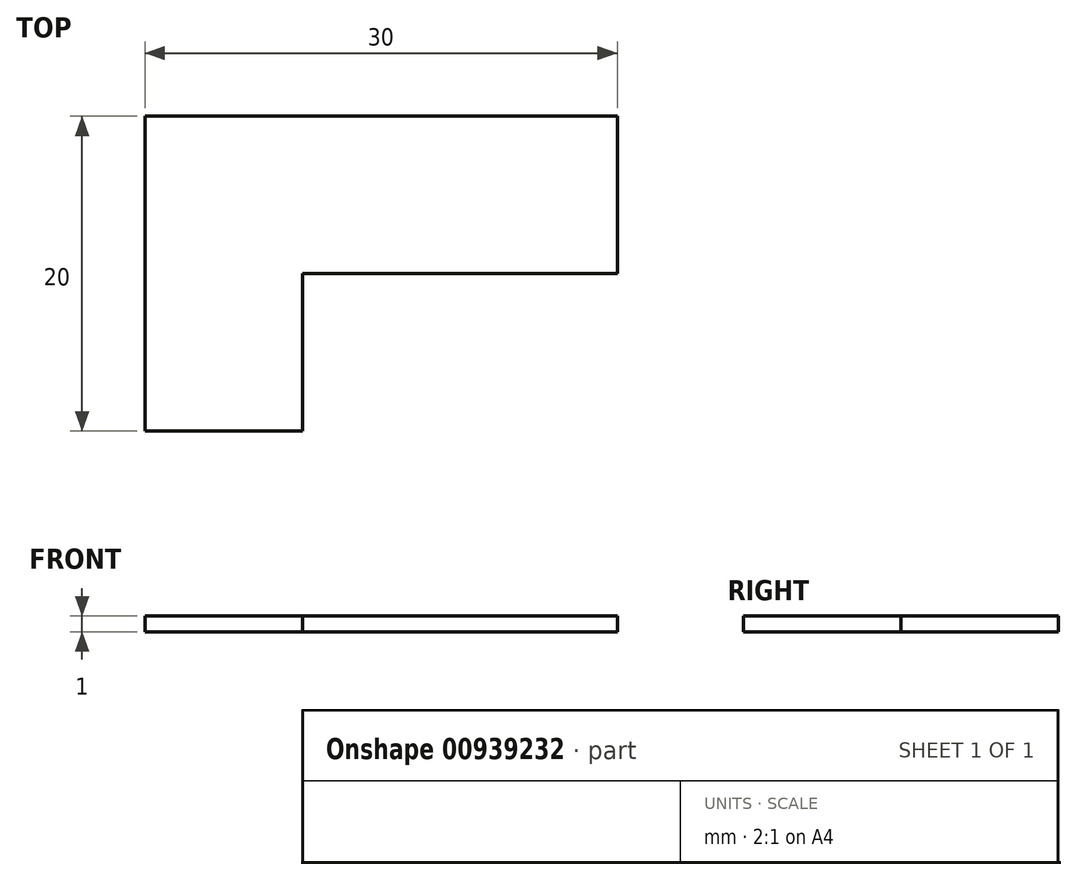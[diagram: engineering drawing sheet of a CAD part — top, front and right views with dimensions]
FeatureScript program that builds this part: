
annotation { "Feature Type Name" : "Feature", "Feature Type Description" : "" }
export const myFeature = defineFeature(function(context is Context, id is Id, definition is map)
    precondition{}
    {
        {
            var Q0;
            Q0=qCreatedBy(makeId("Top.planeOp"),FACE);
            var sketch = newSketch(context, id + "F0", { "sketchPlane" : qUnion([Q0])});
            skLineSegment(sketch, "E0", {"start": v(0, 0) * mm, "end": v(20, 0) * mm});
            skLineSegment(sketch, "E1", {"start": v(20, 0) * mm, "end": v(20, 10) * mm});
            skLineSegment(sketch, "E2", {"start": v(20, 10) * mm, "end": v(-10, 10) * mm});
            skLineSegment(sketch, "E3", {"start": v(-10, 10) * mm, "end": v(-10, -10) * mm});
            skLineSegment(sketch, "E4", {"start": v(-10, -10) * mm, "end": v(0, -10) * mm});
            skLineSegment(sketch, "E5", {"start": v(0, -10) * mm, "end": v(0, 0) * mm});
            skSolve(sketch);
        }
        {
            var Q0;
            Q0=makeQuery(id+"F0.imprint","IMPRINT",FACE,{"disambiguationData":[TD([[makeQuery(id+"F0.imprint","IMPRINT",EDGE,{"derivedFrom":sQuery(id+"F0.wireOp",EDGE,"E0")}),1.0]])]});
            extrude(context, id + "F1", {"entities" : qUnion([Q0]), "depth" : 1 * mm, "offsetDistance" : 25 * mm});
        }
    });
